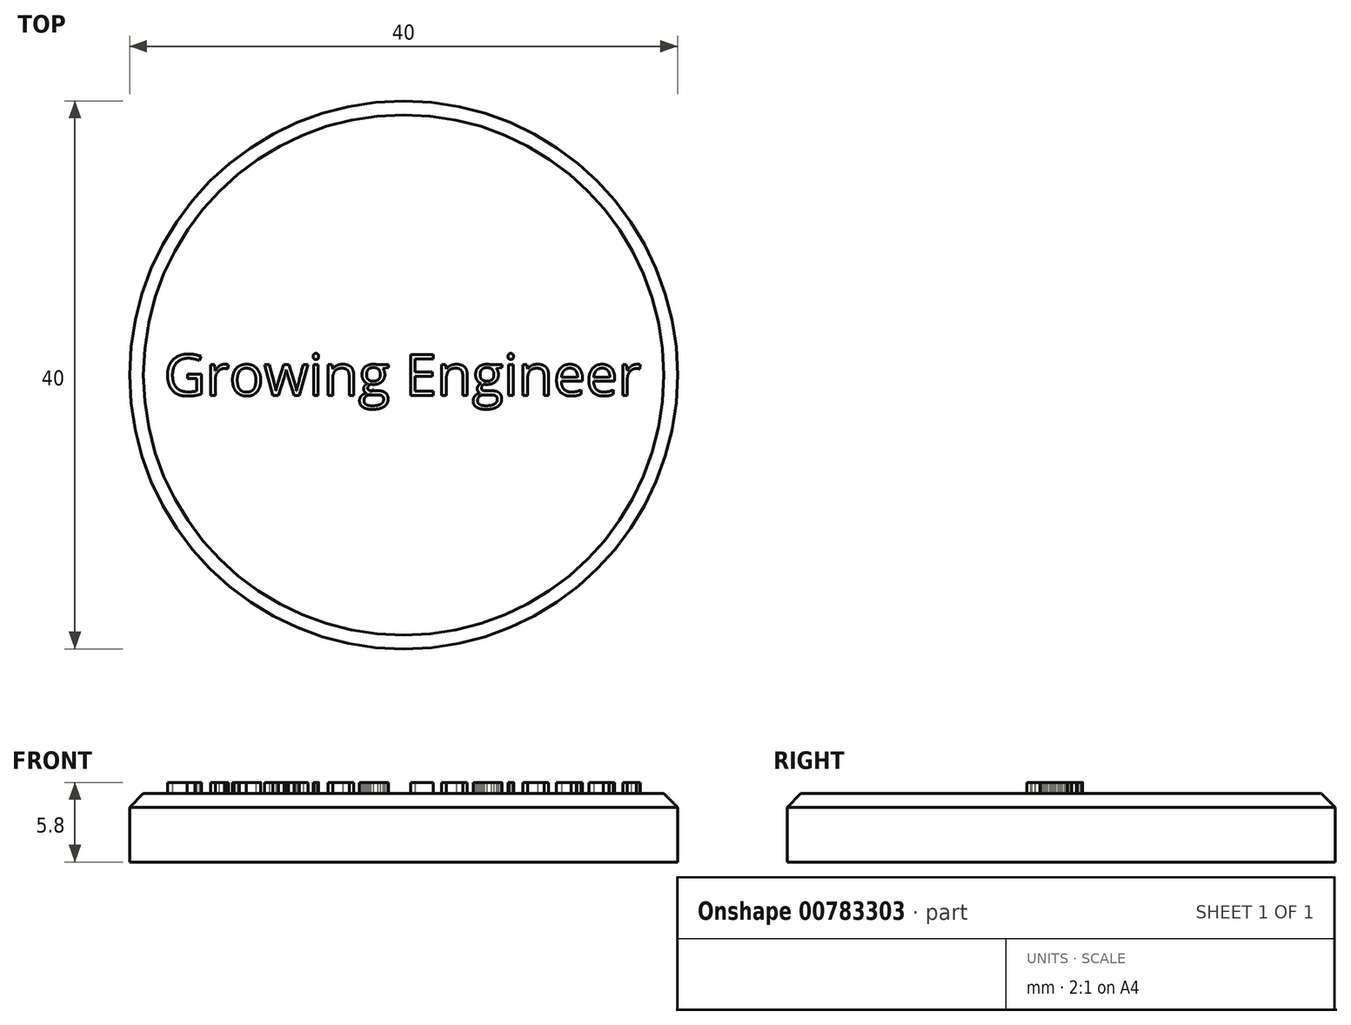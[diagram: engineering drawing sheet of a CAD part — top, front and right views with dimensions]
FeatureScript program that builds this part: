
annotation { "Feature Type Name" : "Feature", "Feature Type Description" : "" }
export const myFeature = defineFeature(function(context is Context, id is Id, definition is map)
    precondition{}
    {
        {
            var Q0;
            Q0=qCreatedBy(makeId("Top.planeOp"),FACE);
            var sketch = newSketch(context, id + "F0", { "sketchPlane" : qUnion([Q0])});
            skCircle(sketch, "E0", {"center": v(0, 0) * mm, "radius": 20 * mm});
            skLineSegment(sketch, "E1", {"start": v(-2.13, 19.89) * mm, "end": v(-1, 23) * mm});
            skLineSegment(sketch, "E2", {"start": v(-1, 23) * mm, "end": v(1, 23) * mm});
            skLineSegment(sketch, "E3", {"start": v(1, 23) * mm, "end": v(2.13, 19.89) * mm});
            skSolve(sketch);
        }
        {
            var Q0;
            {var subQ0=sQuery(id+"F0.wireOp",EDGE,"E0");var subQ1=makeQuery(id+"F0.imprint","INTERSECT",VERTEX,{"derivedFrom":[subQ0,sQuery(id+"F0.wireOp",EDGE,"E1")]});Q0=makeQuery(id+"F0.imprint","IMPRINT",FACE,{"disambiguationData":[TD([[makeQuery(id+"F0.imprint","IMPRINT",EDGE,{"disambiguationData":[TD([[subQ1,1.0]])],"derivedFrom":subQ0}),1.0]])]});}
            var Q1;
            {var subQ0=sQuery(id+"F0.wireOp",EDGE,"E1");Q1=makeQuery(id+"F0.imprint","IMPRINT",FACE,{"disambiguationData":[TD([[makeQuery(id+"F0.imprint","IMPRINT",EDGE,{"derivedFrom":subQ0}),-1.0]])]});}
            extrude(context, id + "F1", {"entities" : qUnion([Q0, Q1]), "depth" : 5 * mm, "offsetDistance" : 25 * mm});
        }
        {
            var Q0;
            Q0=makeQuery(id+"F1.opExtrude","SWEPT_BODY",BODY,{"disambiguationData":[OSD([sQuery(id+"F0.wireOp",EDGE,"E0"),sQuery(id+"F0.wireOp",EDGE,"E1"),sQuery(id+"F0.wireOp",EDGE,"E2"),sQuery(id+"F0.wireOp",EDGE,"E3")])]});
            var Q1;
            Q1=sQuery(id+"F0.wireOp",EDGE,"E0");
            circularPattern(context, id + "F2", {"operationType" : NewBodyOperationType.ADD, "entities" : qUnion([Q0]), "axis" : qUnion([Q1]), "angle" : 360 * degree, "instanceCount" : 18, "equalSpace" : true});
        }
        {
            var Q0;
            Q0=makeQuery(id+"F1.opExtrude","CAP_FACE",FACE,{"disambiguationData":[OSD([sQuery(id+"F0.wireOp",EDGE,"E0"),sQuery(id+"F0.wireOp",EDGE,"E1"),sQuery(id+"F0.wireOp",EDGE,"E2"),sQuery(id+"F0.wireOp",EDGE,"E3")])],"isStart":false});
            var sketch = newSketch(context, id + "F3", { "sketchPlane" : qUnion([Q0])});
            skText(sketch, "E4", { "text": "Growing Engineer", "fontName": "OpenSans-Regular.ttf"});
            const initialGuessF3  = {"E4": [-0.0175, -0.0015, 1, 0, 0.00302]};
            skSetInitialGuess(sketch, initialGuessF3);
            skSolve(sketch);
        }
        {
            var Q0;
            Q0=qSketchRegion(id+"F3",true);
            extrude(context, id + "F4", {"entities" : qUnion([Q0]), "operationType" : NewBodyOperationType.ADD, "depth" : 0.8 * mm, "offsetDistance" : 25 * mm});
        }
        {
            var Q0;
            {var subQ1=sQuery(id+"F0.wireOp",EDGE,"E1");var subQ2=sQuery(id+"F0.wireOp",EDGE,"E0");Q0=makeQuery(id+"F2.boolean.opBoolean","SPLIT",EDGE,{"disambiguationData":[TD([makeQuery(id+"F2.opPattern","COPY",FACE,{"derivedFrom":makeQuery(id+"F1.opExtrude","SWEPT_FACE",FACE,{"disambiguationData":[OSD([subQ1])]}),"instanceName":"12"})])],"derivedFrom":makeQuery(id+"F1.opExtrude","CAP_EDGE",EDGE,{"disambiguationData":[OSD([subQ2])],"isStart":false})});}
            var Q1;
            Q1=makeQuery(id+"F2.opPattern","COPY",EDGE,{"derivedFrom":makeQuery(id+"F1.opExtrude","CAP_EDGE",EDGE,{"disambiguationData":[OSD([sQuery(id+"F0.wireOp",EDGE,"E1")])],"isStart":false}),"instanceName":"12"});
            var Q2;
            Q2=makeQuery(id+"F2.opPattern","COPY",EDGE,{"derivedFrom":makeQuery(id+"F1.opExtrude","CAP_EDGE",EDGE,{"disambiguationData":[OSD([sQuery(id+"F0.wireOp",EDGE,"E2")])],"isStart":false}),"instanceName":"12"});
            var Q3;
            Q3=makeQuery(id+"F2.opPattern","COPY",EDGE,{"derivedFrom":makeQuery(id+"F1.opExtrude","CAP_EDGE",EDGE,{"disambiguationData":[OSD([sQuery(id+"F0.wireOp",EDGE,"E3")])],"isStart":false}),"instanceName":"12"});
            var Q4;
            {var subQ1=sQuery(id+"F0.wireOp",EDGE,"E1");var subQ2=sQuery(id+"F0.wireOp",EDGE,"E0");Q4=makeQuery(id+"F2.boolean.opBoolean","SPLIT",EDGE,{"disambiguationData":[TD([makeQuery(id+"F2.opPattern","COPY",FACE,{"derivedFrom":makeQuery(id+"F1.opExtrude","SWEPT_FACE",FACE,{"disambiguationData":[OSD([subQ1])]}),"instanceName":"11"})])],"derivedFrom":makeQuery(id+"F1.opExtrude","CAP_EDGE",EDGE,{"disambiguationData":[OSD([subQ2])],"isStart":false})});}
            var Q5;
            Q5=makeQuery(id+"F2.opPattern","COPY",EDGE,{"derivedFrom":makeQuery(id+"F1.opExtrude","CAP_EDGE",EDGE,{"disambiguationData":[OSD([sQuery(id+"F0.wireOp",EDGE,"E1")])],"isStart":false}),"instanceName":"11"});
            var Q6;
            Q6=makeQuery(id+"F2.opPattern","COPY",EDGE,{"derivedFrom":makeQuery(id+"F1.opExtrude","CAP_EDGE",EDGE,{"disambiguationData":[OSD([sQuery(id+"F0.wireOp",EDGE,"E2")])],"isStart":false}),"instanceName":"11"});
            var Q7;
            Q7=makeQuery(id+"F2.opPattern","COPY",EDGE,{"derivedFrom":makeQuery(id+"F1.opExtrude","CAP_EDGE",EDGE,{"disambiguationData":[OSD([sQuery(id+"F0.wireOp",EDGE,"E3")])],"isStart":false}),"instanceName":"11"});
            var Q8;
            Q8=makeQuery(id+"F2.opPattern","COPY",EDGE,{"derivedFrom":makeQuery(id+"F1.opExtrude","CAP_EDGE",EDGE,{"disambiguationData":[OSD([sQuery(id+"F0.wireOp",EDGE,"E3")])],"isStart":false}),"instanceName":"13"});
            var Q9;
            Q9=makeQuery(id+"F2.opPattern","COPY",EDGE,{"derivedFrom":makeQuery(id+"F1.opExtrude","CAP_EDGE",EDGE,{"disambiguationData":[OSD([sQuery(id+"F0.wireOp",EDGE,"E2")])],"isStart":false}),"instanceName":"13"});
            var Q10;
            Q10=makeQuery(id+"F2.opPattern","COPY",EDGE,{"derivedFrom":makeQuery(id+"F1.opExtrude","CAP_EDGE",EDGE,{"disambiguationData":[OSD([sQuery(id+"F0.wireOp",EDGE,"E1")])],"isStart":false}),"instanceName":"13"});
            var Q11;
            {var subQ1=sQuery(id+"F0.wireOp",EDGE,"E1");var subQ2=sQuery(id+"F0.wireOp",EDGE,"E0");Q11=makeQuery(id+"F2.boolean.opBoolean","SPLIT",EDGE,{"disambiguationData":[TD([makeQuery(id+"F2.opPattern","COPY",FACE,{"derivedFrom":makeQuery(id+"F1.opExtrude","SWEPT_FACE",FACE,{"disambiguationData":[OSD([subQ1])]}),"instanceName":"13"})])],"derivedFrom":makeQuery(id+"F1.opExtrude","CAP_EDGE",EDGE,{"disambiguationData":[OSD([subQ2])],"isStart":false})});}
            var Q12;
            Q12=makeQuery(id+"F2.opPattern","COPY",EDGE,{"derivedFrom":makeQuery(id+"F1.opExtrude","CAP_EDGE",EDGE,{"disambiguationData":[OSD([sQuery(id+"F0.wireOp",EDGE,"E3")])],"isStart":false}),"instanceName":"14"});
            var Q13;
            Q13=makeQuery(id+"F2.opPattern","COPY",EDGE,{"derivedFrom":makeQuery(id+"F1.opExtrude","CAP_EDGE",EDGE,{"disambiguationData":[OSD([sQuery(id+"F0.wireOp",EDGE,"E2")])],"isStart":false}),"instanceName":"14"});
            var Q14;
            Q14=makeQuery(id+"F2.opPattern","COPY",EDGE,{"derivedFrom":makeQuery(id+"F1.opExtrude","CAP_EDGE",EDGE,{"disambiguationData":[OSD([sQuery(id+"F0.wireOp",EDGE,"E1")])],"isStart":false}),"instanceName":"14"});
            var Q15;
            {var subQ1=sQuery(id+"F0.wireOp",EDGE,"E1");var subQ2=sQuery(id+"F0.wireOp",EDGE,"E0");Q15=makeQuery(id+"F2.boolean.opBoolean","SPLIT",EDGE,{"disambiguationData":[TD([makeQuery(id+"F2.opPattern","COPY",FACE,{"derivedFrom":makeQuery(id+"F1.opExtrude","SWEPT_FACE",FACE,{"disambiguationData":[OSD([subQ1])]}),"instanceName":"14"})])],"derivedFrom":makeQuery(id+"F1.opExtrude","CAP_EDGE",EDGE,{"disambiguationData":[OSD([subQ2])],"isStart":false})});}
            var Q16;
            Q16=makeQuery(id+"F2.opPattern","COPY",EDGE,{"derivedFrom":makeQuery(id+"F1.opExtrude","CAP_EDGE",EDGE,{"disambiguationData":[OSD([sQuery(id+"F0.wireOp",EDGE,"E3")])],"isStart":false}),"instanceName":"15"});
            var Q17;
            Q17=makeQuery(id+"F2.opPattern","COPY",EDGE,{"derivedFrom":makeQuery(id+"F1.opExtrude","CAP_EDGE",EDGE,{"disambiguationData":[OSD([sQuery(id+"F0.wireOp",EDGE,"E2")])],"isStart":false}),"instanceName":"15"});
            var Q18;
            Q18=makeQuery(id+"F2.opPattern","COPY",EDGE,{"derivedFrom":makeQuery(id+"F1.opExtrude","CAP_EDGE",EDGE,{"disambiguationData":[OSD([sQuery(id+"F0.wireOp",EDGE,"E1")])],"isStart":false}),"instanceName":"15"});
            var Q19;
            {var subQ1=sQuery(id+"F0.wireOp",EDGE,"E1");var subQ2=sQuery(id+"F0.wireOp",EDGE,"E0");Q19=makeQuery(id+"F2.boolean.opBoolean","SPLIT",EDGE,{"disambiguationData":[TD([makeQuery(id+"F2.opPattern","COPY",FACE,{"derivedFrom":makeQuery(id+"F1.opExtrude","SWEPT_FACE",FACE,{"disambiguationData":[OSD([subQ1])]}),"instanceName":"15"})])],"derivedFrom":makeQuery(id+"F1.opExtrude","CAP_EDGE",EDGE,{"disambiguationData":[OSD([subQ2])],"isStart":false})});}
            var Q20;
            Q20=makeQuery(id+"F2.opPattern","COPY",EDGE,{"derivedFrom":makeQuery(id+"F1.opExtrude","CAP_EDGE",EDGE,{"disambiguationData":[OSD([sQuery(id+"F0.wireOp",EDGE,"E3")])],"isStart":false}),"instanceName":"16"});
            var Q21;
            Q21=makeQuery(id+"F2.opPattern","COPY",EDGE,{"derivedFrom":makeQuery(id+"F1.opExtrude","CAP_EDGE",EDGE,{"disambiguationData":[OSD([sQuery(id+"F0.wireOp",EDGE,"E2")])],"isStart":false}),"instanceName":"16"});
            var Q22;
            Q22=makeQuery(id+"F2.opPattern","COPY",EDGE,{"derivedFrom":makeQuery(id+"F1.opExtrude","CAP_EDGE",EDGE,{"disambiguationData":[OSD([sQuery(id+"F0.wireOp",EDGE,"E1")])],"isStart":false}),"instanceName":"16"});
            var Q23;
            {var subQ1=sQuery(id+"F0.wireOp",EDGE,"E1");var subQ2=sQuery(id+"F0.wireOp",EDGE,"E0");Q23=makeQuery(id+"F2.boolean.opBoolean","SPLIT",EDGE,{"disambiguationData":[TD([makeQuery(id+"F2.opPattern","COPY",FACE,{"derivedFrom":makeQuery(id+"F1.opExtrude","SWEPT_FACE",FACE,{"disambiguationData":[OSD([subQ1])]}),"instanceName":"16"})])],"derivedFrom":makeQuery(id+"F1.opExtrude","CAP_EDGE",EDGE,{"disambiguationData":[OSD([subQ2])],"isStart":false})});}
            var Q24;
            Q24=makeQuery(id+"F2.opPattern","COPY",EDGE,{"derivedFrom":makeQuery(id+"F1.opExtrude","CAP_EDGE",EDGE,{"disambiguationData":[OSD([sQuery(id+"F0.wireOp",EDGE,"E3")])],"isStart":false}),"instanceName":"17"});
            var Q25;
            Q25=makeQuery(id+"F2.opPattern","COPY",EDGE,{"derivedFrom":makeQuery(id+"F1.opExtrude","CAP_EDGE",EDGE,{"disambiguationData":[OSD([sQuery(id+"F0.wireOp",EDGE,"E1")])],"isStart":false}),"instanceName":"17"});
            var Q26;
            {var subQ0=sQuery(id+"F0.wireOp",EDGE,"E3");var subQ2=sQuery(id+"F0.wireOp",EDGE,"E0");Q26=makeQuery(id+"F2.boolean.opBoolean","SPLIT",EDGE,{"disambiguationData":[TD([makeQuery(id+"F1.opExtrude","SWEPT_FACE",FACE,{"disambiguationData":[OSD([subQ0])]})])],"derivedFrom":makeQuery(id+"F1.opExtrude","CAP_EDGE",EDGE,{"disambiguationData":[OSD([subQ2])],"isStart":false})});}
            var Q27;
            Q27=makeQuery(id+"F1.opExtrude","CAP_EDGE",EDGE,{"disambiguationData":[OSD([sQuery(id+"F0.wireOp",EDGE,"E3")])],"isStart":false});
            var Q28;
            Q28=makeQuery(id+"F1.opExtrude","CAP_EDGE",EDGE,{"disambiguationData":[OSD([sQuery(id+"F0.wireOp",EDGE,"E1")])],"isStart":false});
            var Q29;
            {var subQ1=sQuery(id+"F0.wireOp",EDGE,"E1");var subQ2=sQuery(id+"F0.wireOp",EDGE,"E0");Q29=makeQuery(id+"F2.boolean.opBoolean","SPLIT",EDGE,{"disambiguationData":[TD([makeQuery(id+"F1.opExtrude","SWEPT_FACE",FACE,{"disambiguationData":[OSD([subQ1])]})])],"derivedFrom":makeQuery(id+"F1.opExtrude","CAP_EDGE",EDGE,{"disambiguationData":[OSD([subQ2])],"isStart":false})});}
            var Q30;
            Q30=makeQuery(id+"F2.opPattern","COPY",EDGE,{"derivedFrom":makeQuery(id+"F1.opExtrude","CAP_EDGE",EDGE,{"disambiguationData":[OSD([sQuery(id+"F0.wireOp",EDGE,"E3")])],"isStart":false}),"instanceName":"1"});
            var Q31;
            Q31=makeQuery(id+"F2.opPattern","COPY",EDGE,{"derivedFrom":makeQuery(id+"F1.opExtrude","CAP_EDGE",EDGE,{"disambiguationData":[OSD([sQuery(id+"F0.wireOp",EDGE,"E1")])],"isStart":false}),"instanceName":"1"});
            var Q32;
            {var subQ1=sQuery(id+"F0.wireOp",EDGE,"E1");var subQ2=sQuery(id+"F0.wireOp",EDGE,"E0");Q32=makeQuery(id+"F2.boolean.opBoolean","SPLIT",EDGE,{"disambiguationData":[TD([makeQuery(id+"F2.opPattern","COPY",FACE,{"derivedFrom":makeQuery(id+"F1.opExtrude","SWEPT_FACE",FACE,{"disambiguationData":[OSD([subQ1])]}),"instanceName":"1"})])],"derivedFrom":makeQuery(id+"F1.opExtrude","CAP_EDGE",EDGE,{"disambiguationData":[OSD([subQ2])],"isStart":false})});}
            var Q33;
            Q33=makeQuery(id+"F2.opPattern","COPY",EDGE,{"derivedFrom":makeQuery(id+"F1.opExtrude","CAP_EDGE",EDGE,{"disambiguationData":[OSD([sQuery(id+"F0.wireOp",EDGE,"E3")])],"isStart":false}),"instanceName":"2"});
            var Q34;
            Q34=makeQuery(id+"F2.opPattern","COPY",EDGE,{"derivedFrom":makeQuery(id+"F1.opExtrude","CAP_EDGE",EDGE,{"disambiguationData":[OSD([sQuery(id+"F0.wireOp",EDGE,"E1")])],"isStart":false}),"instanceName":"2"});
            var Q35;
            {var subQ1=sQuery(id+"F0.wireOp",EDGE,"E1");var subQ2=sQuery(id+"F0.wireOp",EDGE,"E0");Q35=makeQuery(id+"F2.boolean.opBoolean","SPLIT",EDGE,{"disambiguationData":[TD([makeQuery(id+"F2.opPattern","COPY",FACE,{"derivedFrom":makeQuery(id+"F1.opExtrude","SWEPT_FACE",FACE,{"disambiguationData":[OSD([subQ1])]}),"instanceName":"2"})])],"derivedFrom":makeQuery(id+"F1.opExtrude","CAP_EDGE",EDGE,{"disambiguationData":[OSD([subQ2])],"isStart":false})});}
            var Q36;
            Q36=makeQuery(id+"F2.opPattern","COPY",EDGE,{"derivedFrom":makeQuery(id+"F1.opExtrude","CAP_EDGE",EDGE,{"disambiguationData":[OSD([sQuery(id+"F0.wireOp",EDGE,"E3")])],"isStart":false}),"instanceName":"3"});
            var Q37;
            Q37=makeQuery(id+"F2.opPattern","COPY",EDGE,{"derivedFrom":makeQuery(id+"F1.opExtrude","CAP_EDGE",EDGE,{"disambiguationData":[OSD([sQuery(id+"F0.wireOp",EDGE,"E1")])],"isStart":false}),"instanceName":"3"});
            var Q38;
            {var subQ1=sQuery(id+"F0.wireOp",EDGE,"E1");var subQ2=sQuery(id+"F0.wireOp",EDGE,"E0");Q38=makeQuery(id+"F2.boolean.opBoolean","SPLIT",EDGE,{"disambiguationData":[TD([makeQuery(id+"F2.opPattern","COPY",FACE,{"derivedFrom":makeQuery(id+"F1.opExtrude","SWEPT_FACE",FACE,{"disambiguationData":[OSD([subQ1])]}),"instanceName":"3"})])],"derivedFrom":makeQuery(id+"F1.opExtrude","CAP_EDGE",EDGE,{"disambiguationData":[OSD([subQ2])],"isStart":false})});}
            var Q39;
            Q39=makeQuery(id+"F2.opPattern","COPY",EDGE,{"derivedFrom":makeQuery(id+"F1.opExtrude","CAP_EDGE",EDGE,{"disambiguationData":[OSD([sQuery(id+"F0.wireOp",EDGE,"E3")])],"isStart":false}),"instanceName":"4"});
            var Q40;
            Q40=makeQuery(id+"F2.opPattern","COPY",EDGE,{"derivedFrom":makeQuery(id+"F1.opExtrude","CAP_EDGE",EDGE,{"disambiguationData":[OSD([sQuery(id+"F0.wireOp",EDGE,"E2")])],"isStart":false}),"instanceName":"4"});
            var Q41;
            Q41=makeQuery(id+"F2.opPattern","COPY",EDGE,{"derivedFrom":makeQuery(id+"F1.opExtrude","CAP_EDGE",EDGE,{"disambiguationData":[OSD([sQuery(id+"F0.wireOp",EDGE,"E1")])],"isStart":false}),"instanceName":"4"});
            var Q42;
            Q42=makeQuery(id+"F2.opPattern","COPY",EDGE,{"derivedFrom":makeQuery(id+"F1.opExtrude","CAP_EDGE",EDGE,{"disambiguationData":[OSD([sQuery(id+"F0.wireOp",EDGE,"E2")])],"isStart":false}),"instanceName":"3"});
            var Q43;
            Q43=makeQuery(id+"F2.opPattern","COPY",EDGE,{"derivedFrom":makeQuery(id+"F1.opExtrude","CAP_EDGE",EDGE,{"disambiguationData":[OSD([sQuery(id+"F0.wireOp",EDGE,"E2")])],"isStart":false}),"instanceName":"2"});
            var Q44;
            Q44=makeQuery(id+"F2.opPattern","COPY",EDGE,{"derivedFrom":makeQuery(id+"F1.opExtrude","CAP_EDGE",EDGE,{"disambiguationData":[OSD([sQuery(id+"F0.wireOp",EDGE,"E2")])],"isStart":false}),"instanceName":"1"});
            var Q45;
            Q45=makeQuery(id+"F1.opExtrude","CAP_EDGE",EDGE,{"disambiguationData":[OSD([sQuery(id+"F0.wireOp",EDGE,"E2")])],"isStart":false});
            var Q46;
            Q46=makeQuery(id+"F2.opPattern","COPY",EDGE,{"derivedFrom":makeQuery(id+"F1.opExtrude","CAP_EDGE",EDGE,{"disambiguationData":[OSD([sQuery(id+"F0.wireOp",EDGE,"E2")])],"isStart":false}),"instanceName":"17"});
            var Q47;
            {var subQ1=sQuery(id+"F0.wireOp",EDGE,"E1");var subQ2=sQuery(id+"F0.wireOp",EDGE,"E0");Q47=makeQuery(id+"F2.boolean.opBoolean","SPLIT",EDGE,{"disambiguationData":[TD([makeQuery(id+"F2.opPattern","COPY",FACE,{"derivedFrom":makeQuery(id+"F1.opExtrude","SWEPT_FACE",FACE,{"disambiguationData":[OSD([subQ1])]}),"instanceName":"4"})])],"derivedFrom":makeQuery(id+"F1.opExtrude","CAP_EDGE",EDGE,{"disambiguationData":[OSD([subQ2])],"isStart":false})});}
            var Q48;
            Q48=makeQuery(id+"F2.opPattern","COPY",EDGE,{"derivedFrom":makeQuery(id+"F1.opExtrude","CAP_EDGE",EDGE,{"disambiguationData":[OSD([sQuery(id+"F0.wireOp",EDGE,"E3")])],"isStart":false}),"instanceName":"5"});
            var Q49;
            Q49=makeQuery(id+"F2.opPattern","COPY",EDGE,{"derivedFrom":makeQuery(id+"F1.opExtrude","CAP_EDGE",EDGE,{"disambiguationData":[OSD([sQuery(id+"F0.wireOp",EDGE,"E2")])],"isStart":false}),"instanceName":"5"});
            var Q50;
            Q50=makeQuery(id+"F2.opPattern","COPY",EDGE,{"derivedFrom":makeQuery(id+"F1.opExtrude","CAP_EDGE",EDGE,{"disambiguationData":[OSD([sQuery(id+"F0.wireOp",EDGE,"E1")])],"isStart":false}),"instanceName":"5"});
            var Q51;
            {var subQ1=sQuery(id+"F0.wireOp",EDGE,"E1");var subQ2=sQuery(id+"F0.wireOp",EDGE,"E0");Q51=makeQuery(id+"F2.boolean.opBoolean","SPLIT",EDGE,{"disambiguationData":[TD([makeQuery(id+"F2.opPattern","COPY",FACE,{"derivedFrom":makeQuery(id+"F1.opExtrude","SWEPT_FACE",FACE,{"disambiguationData":[OSD([subQ1])]}),"instanceName":"5"})])],"derivedFrom":makeQuery(id+"F1.opExtrude","CAP_EDGE",EDGE,{"disambiguationData":[OSD([subQ2])],"isStart":false})});}
            var Q52;
            Q52=makeQuery(id+"F2.opPattern","COPY",EDGE,{"derivedFrom":makeQuery(id+"F1.opExtrude","CAP_EDGE",EDGE,{"disambiguationData":[OSD([sQuery(id+"F0.wireOp",EDGE,"E3")])],"isStart":false}),"instanceName":"6"});
            var Q53;
            Q53=makeQuery(id+"F2.opPattern","COPY",EDGE,{"derivedFrom":makeQuery(id+"F1.opExtrude","CAP_EDGE",EDGE,{"disambiguationData":[OSD([sQuery(id+"F0.wireOp",EDGE,"E2")])],"isStart":false}),"instanceName":"6"});
            var Q54;
            Q54=makeQuery(id+"F2.opPattern","COPY",EDGE,{"derivedFrom":makeQuery(id+"F1.opExtrude","CAP_EDGE",EDGE,{"disambiguationData":[OSD([sQuery(id+"F0.wireOp",EDGE,"E1")])],"isStart":false}),"instanceName":"6"});
            var Q55;
            {var subQ1=sQuery(id+"F0.wireOp",EDGE,"E1");var subQ2=sQuery(id+"F0.wireOp",EDGE,"E0");Q55=makeQuery(id+"F2.boolean.opBoolean","SPLIT",EDGE,{"disambiguationData":[TD([makeQuery(id+"F2.opPattern","COPY",FACE,{"derivedFrom":makeQuery(id+"F1.opExtrude","SWEPT_FACE",FACE,{"disambiguationData":[OSD([subQ1])]}),"instanceName":"6"})])],"derivedFrom":makeQuery(id+"F1.opExtrude","CAP_EDGE",EDGE,{"disambiguationData":[OSD([subQ2])],"isStart":false})});}
            var Q56;
            Q56=makeQuery(id+"F2.opPattern","COPY",EDGE,{"derivedFrom":makeQuery(id+"F1.opExtrude","CAP_EDGE",EDGE,{"disambiguationData":[OSD([sQuery(id+"F0.wireOp",EDGE,"E3")])],"isStart":false}),"instanceName":"7"});
            var Q57;
            Q57=makeQuery(id+"F2.opPattern","COPY",EDGE,{"derivedFrom":makeQuery(id+"F1.opExtrude","CAP_EDGE",EDGE,{"disambiguationData":[OSD([sQuery(id+"F0.wireOp",EDGE,"E2")])],"isStart":false}),"instanceName":"7"});
            var Q58;
            Q58=makeQuery(id+"F2.opPattern","COPY",EDGE,{"derivedFrom":makeQuery(id+"F1.opExtrude","CAP_EDGE",EDGE,{"disambiguationData":[OSD([sQuery(id+"F0.wireOp",EDGE,"E1")])],"isStart":false}),"instanceName":"7"});
            var Q59;
            {var subQ0=sQuery(id+"F0.wireOp",EDGE,"E1");var subQ2=sQuery(id+"F0.wireOp",EDGE,"E0");Q59=makeQuery(id+"F2.boolean.opBoolean","SPLIT",EDGE,{"disambiguationData":[TD([makeQuery(id+"F2.opPattern","COPY",FACE,{"derivedFrom":makeQuery(id+"F1.opExtrude","SWEPT_FACE",FACE,{"disambiguationData":[OSD([subQ0])]}),"instanceName":"7"})])],"derivedFrom":makeQuery(id+"F1.opExtrude","CAP_EDGE",EDGE,{"disambiguationData":[OSD([subQ2])],"isStart":false})});}
            var Q60;
            Q60=makeQuery(id+"F2.opPattern","COPY",EDGE,{"derivedFrom":makeQuery(id+"F1.opExtrude","CAP_EDGE",EDGE,{"disambiguationData":[OSD([sQuery(id+"F0.wireOp",EDGE,"E3")])],"isStart":false}),"instanceName":"8"});
            var Q61;
            Q61=makeQuery(id+"F2.opPattern","COPY",EDGE,{"derivedFrom":makeQuery(id+"F1.opExtrude","CAP_EDGE",EDGE,{"disambiguationData":[OSD([sQuery(id+"F0.wireOp",EDGE,"E2")])],"isStart":false}),"instanceName":"8"});
            var Q62;
            Q62=makeQuery(id+"F2.opPattern","COPY",EDGE,{"derivedFrom":makeQuery(id+"F1.opExtrude","CAP_EDGE",EDGE,{"disambiguationData":[OSD([sQuery(id+"F0.wireOp",EDGE,"E1")])],"isStart":false}),"instanceName":"8"});
            var Q63;
            {var subQ1=sQuery(id+"F0.wireOp",EDGE,"E1");var subQ2=sQuery(id+"F0.wireOp",EDGE,"E0");Q63=makeQuery(id+"F2.boolean.opBoolean","SPLIT",EDGE,{"disambiguationData":[TD([makeQuery(id+"F2.opPattern","COPY",FACE,{"derivedFrom":makeQuery(id+"F1.opExtrude","SWEPT_FACE",FACE,{"disambiguationData":[OSD([subQ1])]}),"instanceName":"8"})])],"derivedFrom":makeQuery(id+"F1.opExtrude","CAP_EDGE",EDGE,{"disambiguationData":[OSD([subQ2])],"isStart":false})});}
            var Q64;
            Q64=makeQuery(id+"F2.opPattern","COPY",EDGE,{"derivedFrom":makeQuery(id+"F1.opExtrude","CAP_EDGE",EDGE,{"disambiguationData":[OSD([sQuery(id+"F0.wireOp",EDGE,"E3")])],"isStart":false}),"instanceName":"9"});
            var Q65;
            Q65=makeQuery(id+"F2.opPattern","COPY",EDGE,{"derivedFrom":makeQuery(id+"F1.opExtrude","CAP_EDGE",EDGE,{"disambiguationData":[OSD([sQuery(id+"F0.wireOp",EDGE,"E2")])],"isStart":false}),"instanceName":"9"});
            var Q66;
            Q66=makeQuery(id+"F2.opPattern","COPY",EDGE,{"derivedFrom":makeQuery(id+"F1.opExtrude","CAP_EDGE",EDGE,{"disambiguationData":[OSD([sQuery(id+"F0.wireOp",EDGE,"E1")])],"isStart":false}),"instanceName":"9"});
            var Q67;
            {var subQ1=sQuery(id+"F0.wireOp",EDGE,"E1");var subQ2=sQuery(id+"F0.wireOp",EDGE,"E0");Q67=makeQuery(id+"F2.boolean.opBoolean","SPLIT",EDGE,{"disambiguationData":[TD([makeQuery(id+"F2.opPattern","COPY",FACE,{"derivedFrom":makeQuery(id+"F1.opExtrude","SWEPT_FACE",FACE,{"disambiguationData":[OSD([subQ1])]}),"instanceName":"9"})])],"derivedFrom":makeQuery(id+"F1.opExtrude","CAP_EDGE",EDGE,{"disambiguationData":[OSD([subQ2])],"isStart":false})});}
            var Q68;
            Q68=makeQuery(id+"F2.opPattern","COPY",EDGE,{"derivedFrom":makeQuery(id+"F1.opExtrude","CAP_EDGE",EDGE,{"disambiguationData":[OSD([sQuery(id+"F0.wireOp",EDGE,"E3")])],"isStart":false}),"instanceName":"10"});
            var Q69;
            Q69=makeQuery(id+"F2.opPattern","COPY",EDGE,{"derivedFrom":makeQuery(id+"F1.opExtrude","CAP_EDGE",EDGE,{"disambiguationData":[OSD([sQuery(id+"F0.wireOp",EDGE,"E2")])],"isStart":false}),"instanceName":"10"});
            var Q70;
            Q70=makeQuery(id+"F2.opPattern","COPY",EDGE,{"derivedFrom":makeQuery(id+"F1.opExtrude","CAP_EDGE",EDGE,{"disambiguationData":[OSD([sQuery(id+"F0.wireOp",EDGE,"E1")])],"isStart":false}),"instanceName":"10"});
            var Q71;
            {var subQ1=sQuery(id+"F0.wireOp",EDGE,"E1");var subQ2=sQuery(id+"F0.wireOp",EDGE,"E0");Q71=makeQuery(id+"F2.boolean.opBoolean","SPLIT",EDGE,{"disambiguationData":[TD([makeQuery(id+"F2.opPattern","COPY",FACE,{"derivedFrom":makeQuery(id+"F1.opExtrude","SWEPT_FACE",FACE,{"disambiguationData":[OSD([subQ1])]}),"instanceName":"10"})])],"derivedFrom":makeQuery(id+"F1.opExtrude","CAP_EDGE",EDGE,{"disambiguationData":[OSD([subQ2])],"isStart":false})});}
            chamfer(context, id + "F5", {"entities" : qUnion([Q0, Q1, Q2, Q3, Q4, Q5, Q6, Q7, Q8, Q9, Q10, Q11, Q12, Q13, Q14, Q15, Q16, Q17, Q18, Q19, Q20, Q21, Q22, Q23, Q24, Q25, Q26, Q27, Q28, Q29, Q30, Q31, Q32, Q33, Q34, Q35, Q36, Q37, Q38, Q39, Q40, Q41, Q42, Q43, Q44, Q45, Q46, Q47, Q48, Q49, Q50, Q51, Q52, Q53, Q54, Q55, Q56, Q57, Q58, Q59, Q60, Q61, Q62, Q63, Q64, Q65, Q66, Q67, Q68, Q69, Q70, Q71]), "width" : 1 * mm, "tangentPropagation" : true});
        }
    });
